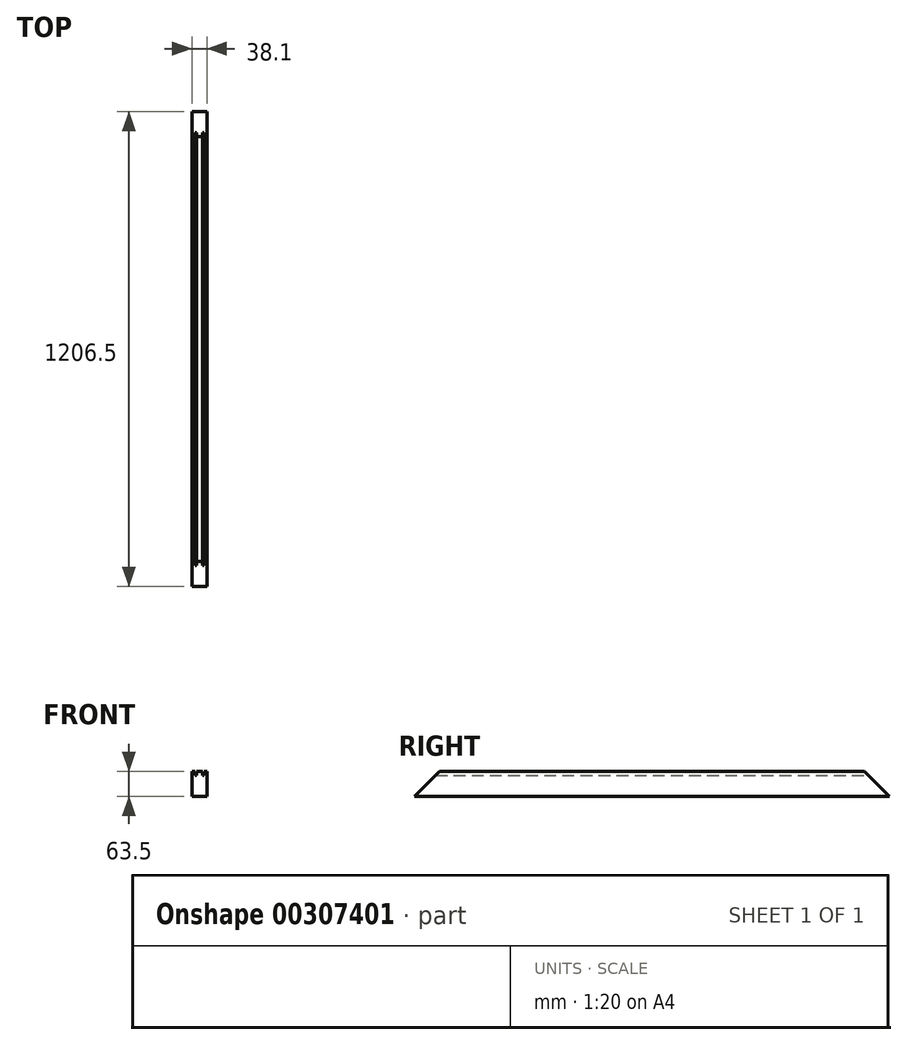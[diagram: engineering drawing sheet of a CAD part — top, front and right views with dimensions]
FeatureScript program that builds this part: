
annotation { "Feature Type Name" : "Feature", "Feature Type Description" : "" }
export const myFeature = defineFeature(function(context is Context, id is Id, definition is map)
    precondition{}
    {
        {
            var Q0;
            Q0=qCreatedBy(makeId("Front.planeOp"),FACE);
            var sketch = newSketch(context, id + "F0", { "sketchPlane" : qUnion([Q0])});
            skLineSegment(sketch, "E0.bottom", {"start": v(19.05, -31.75) * mm, "end": v(-19.05, -31.75) * mm});
            skLineSegment(sketch, "E0.top", {"start": v(19.05, 31.75) * mm, "end": v(-19.05, 31.75) * mm});
            skLineSegment(sketch, "E0.left", {"start": v(19.05, -31.75) * mm, "end": v(19.05, 31.75) * mm});
            skLineSegment(sketch, "E0.right", {"start": v(-19.05, -31.75) * mm, "end": v(-19.05, 31.75) * mm});
            skPoint(sketch, "E0.middle", {"position": v(0, 0) * mm});
            skLineSegment(sketch, "E1.bottom", {"start": v(11.11, 21.59) * mm, "end": v(7.94, 21.59) * mm});
            skLineSegment(sketch, "E1.top", {"start": v(11.11, 31.75) * mm, "end": v(7.94, 31.75) * mm});
            skLineSegment(sketch, "E1.left", {"start": v(11.11, 21.59) * mm, "end": v(11.11, 31.75) * mm});
            skLineSegment(sketch, "E1.right", {"start": v(7.94, 21.59) * mm, "end": v(7.94, 31.75) * mm});
            skPoint(sketch, "E1.middle", {"position": v(9.53, 26.67) * mm});
            skLineSegment(sketch, "E2.bottom", {"start": v(-7.94, 21.59) * mm, "end": v(-11.11, 21.59) * mm});
            skLineSegment(sketch, "E2.top", {"start": v(-7.94, 31.75) * mm, "end": v(-11.11, 31.75) * mm});
            skLineSegment(sketch, "E2.left", {"start": v(-7.94, 21.59) * mm, "end": v(-7.94, 31.75) * mm});
            skLineSegment(sketch, "E2.right", {"start": v(-11.11, 21.59) * mm, "end": v(-11.11, 31.75) * mm});
            skPoint(sketch, "E2.middle", {"position": v(-9.53, 26.67) * mm});
            skSolve(sketch);
        }
        {
            var Q0;
            Q0=makeQuery(id+"F0.imprint","IMPRINT",FACE,{"disambiguationData":[TD([[makeQuery(id+"F0.imprint","IMPRINT",EDGE,{"derivedFrom":sQuery(id+"F0.wireOp",EDGE,"E0.bottom")}),-1.0]])]});
            extrude(context, id + "F1", {"entities" : qUnion([Q0]), "endBound" : BoundingType.SYMMETRIC, "depth" : 1206.5 * mm});
        }
        {
            var Q0;
            Q0=makeQuery(id+"F1.opExtrude","SWEPT_FACE",FACE,{"disambiguationData":[OSD([sQuery(id+"F0.wireOp",EDGE,"E0.right")])]});
            var sketch = newSketch(context, id + "F2", { "sketchPlane" : qUnion([Q0])});
            skLineSegment(sketch, "E3", {"start": v(603.25, -31.75) * mm, "end": v(539.75, 31.75) * mm});
            skLineSegment(sketch, "E4", {"start": v(539.75, 31.75) * mm, "end": v(603.25, 31.75) * mm});
            skLineSegment(sketch, "E5", {"start": v(603.25, 31.75) * mm, "end": v(603.25, -31.75) * mm});
            skLineSegment(sketch, "E6", {"start": v(-603.25, -31.75) * mm, "end": v(-539.75, 31.75) * mm});
            skLineSegment(sketch, "E7", {"start": v(-539.75, 31.75) * mm, "end": v(-603.25, 31.75) * mm});
            skLineSegment(sketch, "E8", {"start": v(-603.25, 31.75) * mm, "end": v(-603.25, -31.75) * mm});
            skSolve(sketch);
        }
        {
            var Q0;
            Q0=qSketchRegion(id+"F2",true);
            extrude(context, id + "F3", {"entities" : qUnion([Q0]), "operationType" : NewBodyOperationType.REMOVE, "endBound" : BoundingType.THROUGH_ALL, "oppositeDirection" : true, "depth" : 25.4 * mm});
        }
    });
